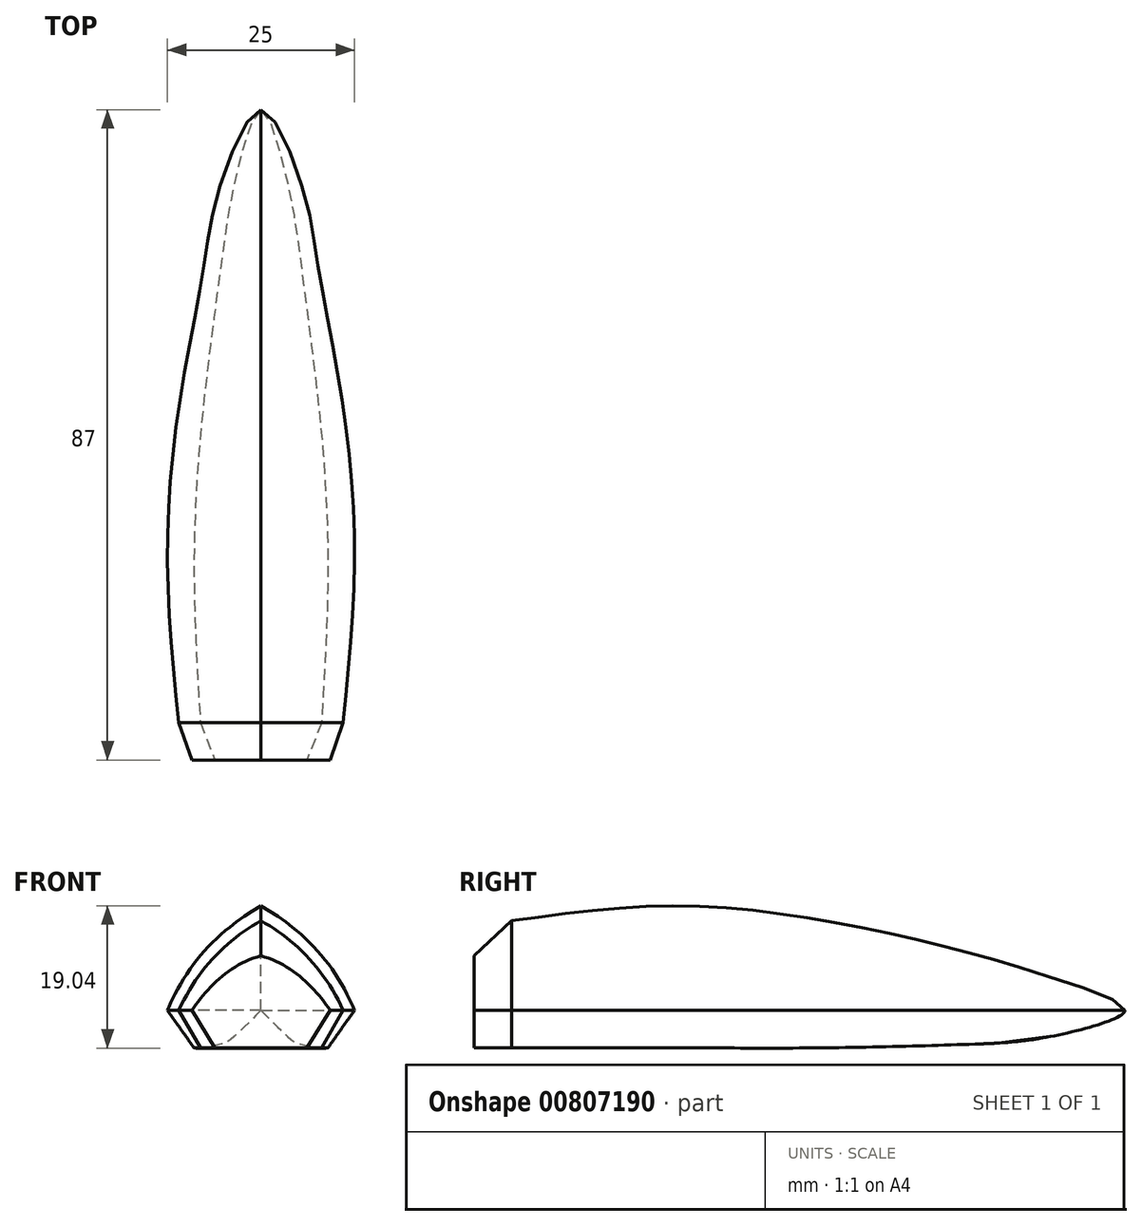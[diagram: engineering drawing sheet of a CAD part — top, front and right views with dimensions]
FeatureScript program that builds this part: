
annotation { "Feature Type Name" : "Feature", "Feature Type Description" : "" }
export const myFeature = defineFeature(function(context is Context, id is Id, definition is map)
    precondition{}
    {
        {
            var Q0;
            Q0=qCreatedBy(makeId("Front.planeOp"),FACE);
            cPlane(context, id + "F0", {"entities" : qUnion([Q0]), "cplaneType" : CPlaneType.OFFSET, "offset" : 43.5 * mm, "oppositeDirection" : true, "width" : 152.4 * mm, "height" : 152.4 * mm});
        }
        {
            var Q0;
            Q0=qCreatedBy(id+"F0.planeOp",FACE);
            cPlane(context, id + "F1", {"entities" : qUnion([Q0]), "cplaneType" : CPlaneType.OFFSET, "offset" : 10 * mm, "width" : 150 * mm, "height" : 150 * mm});
        }
        {
            var Q0;
            Q0=qCreatedBy(id+"F0.planeOp",FACE);
            cPlane(context, id + "F2", {"entities" : qUnion([Q0]), "cplaneType" : CPlaneType.OFFSET, "offset" : 20 * mm, "width" : 150 * mm, "height" : 150 * mm});
        }
        {
            var Q0;
            Q0=qCreatedBy(id+"F0.planeOp",FACE);
            cPlane(context, id + "F3", {"entities" : qUnion([Q0]), "cplaneType" : CPlaneType.OFFSET, "offset" : 40 * mm, "width" : 150 * mm, "height" : 150 * mm});
        }
        {
            var Q0;
            Q0=qCreatedBy(id+"F0.planeOp",FACE);
            cPlane(context, id + "F4", {"entities" : qUnion([Q0]), "cplaneType" : CPlaneType.OFFSET, "offset" : 60 * mm, "width" : 150 * mm, "height" : 150 * mm});
        }
        {
            var Q0;
            Q0=qCreatedBy(id+"F0.planeOp",FACE);
            cPlane(context, id + "F5", {"entities" : qUnion([Q0]), "cplaneType" : CPlaneType.OFFSET, "offset" : 82 * mm, "width" : 150 * mm, "height" : 150 * mm});
        }
        {
            var Q0;
            Q0=qCreatedBy(id+"F0.planeOp",FACE);
            cPlane(context, id + "F6", {"entities" : qUnion([Q0]), "cplaneType" : CPlaneType.OFFSET, "offset" : 87 * mm, "width" : 150 * mm, "height" : 150 * mm});
        }
        {
            var Q0;
            Q0=qCreatedBy(id+"F0.planeOp",FACE);
            var sketch = newSketch(context, id + "F7", { "sketchPlane" : qUnion([Q0])});
            skPoint(sketch, "E0", {"position": v(0, 0) * mm});
            skSolve(sketch);
        }
        {
            var Q0;
            Q0=qCreatedBy(id+"F1.planeOp",FACE);
            var sketch = newSketch(context, id + "F8", { "sketchPlane" : qUnion([Q0])});
            skLineSegment(sketch, "E1", {"start": v(0, -3.5) * mm, "end": v(0, 4.47) * mm, "construction": true});
            skLineSegment(sketch, "E2", {"start": v(5.4, 0) * mm, "end": v(-5.4, 0) * mm, "construction": true});
            skLineSegment(sketch, "E3", {"start": v(5.4, 0) * mm, "end": v(3.6, -3.5) * mm});
            skLineSegment(sketch, "E4", {"start": v(3.6, -3.5) * mm, "end": v(-3.6, -3.5) * mm});
            skLineSegment(sketch, "E5", {"start": v(-3.6, -3.5) * mm, "end": v(-5.4, 0) * mm});
            skPoint(sketch, "E6", {"position": v(0, -3.5) * mm});
            skFitSpline(sketch, "E7", {"points": [v(-5.4, 0) * mm, v(0, 4.47) * mm], "startDerivative": vector(1.5, 3.9) * mm, "endDerivative": vector(9, 1.5) * mm});
            skFitSpline(sketch, "E8.MirrorCS", {"points": [v(5.4, 0) * mm, v(0, 4.47) * mm], "startDerivative": vector(-1.5, 3.9) * mm, "endDerivative": vector(-9, 1.5) * mm});
            skSolve(sketch);
        }
        {
            var Q0;
            Q0=qCreatedBy(id+"F2.planeOp",FACE);
            var sketch = newSketch(context, id + "F9", { "sketchPlane" : qUnion([Q0])});
            skLineSegment(sketch, "E9", {"start": v(0, 7.5) * mm, "end": v(0, -4.5) * mm, "construction": true});
            skLineSegment(sketch, "E10", {"start": v(-7.5, 0) * mm, "end": v(7.5, 0) * mm, "construction": true});
            skLineSegment(sketch, "E11", {"start": v(-7.5, 0) * mm, "end": v(-5.25, -4.5) * mm});
            skLineSegment(sketch, "E12", {"start": v(-5.25, -4.5) * mm, "end": v(5.25, -4.5) * mm});
            skLineSegment(sketch, "E13", {"start": v(5.25, -4.5) * mm, "end": v(7.5, 0) * mm});
            skFitSpline(sketch, "E14", {"points": [v(-7.5, 0) * mm, v(0, 7.5) * mm], "startDerivative": vector(6, 9) * mm, "endDerivative": vector(12, 6) * mm});
            skFitSpline(sketch, "E15.MirrorCS", {"points": [v(7.5, 0) * mm, v(0, 7.5) * mm], "startDerivative": vector(-6, 9) * mm, "endDerivative": vector(-12, 6) * mm});
            skSolve(sketch);
        }
        {
            var Q0;
            Q0=qCreatedBy(id+"F3.planeOp",FACE);
            var sketch = newSketch(context, id + "F10", { "sketchPlane" : qUnion([Q0])});
            skLineSegment(sketch, "E16", {"start": v(0, 11.95) * mm, "end": v(0, -5) * mm, "construction": true});
            skLineSegment(sketch, "E17", {"start": v(-11, 0) * mm, "end": v(11, 0) * mm, "construction": true});
            skLineSegment(sketch, "E18", {"start": v(-11, 0) * mm, "end": v(-7.75, -5) * mm});
            skLineSegment(sketch, "E19", {"start": v(-7.75, -5) * mm, "end": v(7.75, -5) * mm});
            skLineSegment(sketch, "E20", {"start": v(7.75, -5) * mm, "end": v(11, 0) * mm});
            skFitSpline(sketch, "E21", {"points": [v(-11, 0) * mm, v(0, 11.95) * mm], "startDerivative": vector(6, 15) * mm, "endDerivative": vector(15, 7.5) * mm});
            skFitSpline(sketch, "E22.MirrorCS", {"points": [v(11, 0) * mm, v(0, 11.95) * mm], "startDerivative": vector(-6, 15) * mm, "endDerivative": vector(-15, 7.5) * mm});
            skSolve(sketch);
        }
        {
            var Q0;
            Q0=qCreatedBy(id+"F4.planeOp",FACE);
            var sketch = newSketch(context, id + "F11", { "sketchPlane" : qUnion([Q0])});
            skLineSegment(sketch, "E23", {"start": v(-12.5, 0) * mm, "end": v(12.5, 0) * mm, "construction": true});
            skLineSegment(sketch, "E24", {"start": v(0, -5) * mm, "end": v(0, 14) * mm, "construction": true});
            skLineSegment(sketch, "E25", {"start": v(-12.5, 0) * mm, "end": v(-8.95, -5) * mm});
            skLineSegment(sketch, "E26", {"start": v(-8.95, -5) * mm, "end": v(8.95, -5) * mm});
            skLineSegment(sketch, "E27", {"start": v(8.95, -5) * mm, "end": v(12.5, 0) * mm});
            skFitSpline(sketch, "E28", {"points": [v(-12.5, 0) * mm, v(0, 14) * mm], "startDerivative": vector(7.5, 18) * mm, "endDerivative": vector(18, 10.5) * mm});
            skFitSpline(sketch, "E29.MirrorCS", {"points": [v(12.5, 0) * mm, v(0, 14) * mm], "startDerivative": vector(-7.5, 18) * mm, "endDerivative": vector(-18, 10.5) * mm});
            skSolve(sketch);
        }
        {
            var Q0;
            Q0=qCreatedBy(id+"F5.planeOp",FACE);
            var sketch = newSketch(context, id + "F12", { "sketchPlane" : qUnion([Q0])});
            skLineSegment(sketch, "E30", {"start": v(0, 12) * mm, "end": v(0, -5) * mm, "construction": true});
            skLineSegment(sketch, "E31", {"start": v(11, 0) * mm, "end": v(-11, 0) * mm, "construction": true});
            skLineSegment(sketch, "E32", {"start": v(-11, 0) * mm, "end": v(-8.1, -5) * mm});
            skLineSegment(sketch, "E33", {"start": v(-8.1, -5) * mm, "end": v(8.1, -5) * mm});
            skLineSegment(sketch, "E34", {"start": v(8.1, -5) * mm, "end": v(11, 0) * mm});
            skFitSpline(sketch, "E35", {"points": [v(-11, 0) * mm, v(0, 12) * mm], "startDerivative": vector(7.5, 16.5) * mm, "endDerivative": vector(13.5, 7.5) * mm});
            skFitSpline(sketch, "E36.MirrorCS", {"points": [v(11, 0) * mm, v(0, 12) * mm], "startDerivative": vector(-7.5, 16.5) * mm, "endDerivative": vector(-13.5, 7.5) * mm});
            skSolve(sketch);
        }
        {
            var Q0;
            Q0=qCreatedBy(id+"F6.planeOp",FACE);
            var sketch = newSketch(context, id + "F13", { "sketchPlane" : qUnion([Q0])});
            skLineSegment(sketch, "E37", {"start": v(0, 7.3) * mm, "end": v(0, -5) * mm, "construction": true});
            skLineSegment(sketch, "E38", {"start": v(-9.25, 0) * mm, "end": v(9.25, 0) * mm, "construction": true});
            skLineSegment(sketch, "E39", {"start": v(-9.25, 0) * mm, "end": v(-6.15, -5) * mm});
            skLineSegment(sketch, "E40", {"start": v(-6.15, -5) * mm, "end": v(6.15, -5) * mm});
            skLineSegment(sketch, "E41", {"start": v(6.15, -5) * mm, "end": v(9.25, 0) * mm});
            skFitSpline(sketch, "E42", {"points": [v(-9.25, 0) * mm, v(0, 7.3) * mm], "startDerivative": vector(6, 9) * mm, "endDerivative": vector(12, 3) * mm});
            skFitSpline(sketch, "E43.MirrorCS", {"points": [v(9.25, 0) * mm, v(0, 7.3) * mm], "startDerivative": vector(-6, 9) * mm, "endDerivative": vector(-12, 3) * mm});
            skSolve(sketch);
        }
        {
            var Q0;
            Q0=qCreatedBy(makeId("Right.planeOp"),FACE);
            var sketch = newSketch(context, id + "F14", { "sketchPlane" : qUnion([Q0])});
            skPoint(sketch, "E44.0", {"position": v(23.5, 7.5) * mm});
            skPoint(sketch, "E45.0", {"position": v(3.5, 11.95) * mm});
            skPoint(sketch, "E46.0", {"position": v(43.5, 0) * mm});
            skPoint(sketch, "E47.0", {"position": v(-16.5, 14) * mm});
            skPoint(sketch, "E48.0", {"position": v(-38.5, 12) * mm});
            skFitSpline(sketch, "E49", {"points": [v(43.5, 0) * mm, v(23.5, 7.54) * mm, v(3.5, 11.95) * mm, v(-16.5, 14) * mm, v(-38.5, 12) * mm], "startDerivative": vector(-69.58, 39.92) * mm, "endDerivative": vector(-83.95, -26.6) * mm});
            skSolve(sketch);
        }
        {
            var Q0;
            Q0=sQuery(id+"F7.wireOp",VERTEX,"E0");
            var Q1;
            Q1=makeQuery(id+"F8.imprint","IMPRINT",FACE,{"disambiguationData":[TD([[makeQuery(id+"F8.imprint","IMPRINT",EDGE,{"derivedFrom":sQuery(id+"F8.wireOp",EDGE,"E3")}),-1.0]])]});
            var Q2;
            Q2=makeQuery(id+"F9.imprint","IMPRINT",FACE,{"disambiguationData":[TD([[makeQuery(id+"F9.imprint","IMPRINT",EDGE,{"derivedFrom":sQuery(id+"F9.wireOp",EDGE,"E11")}),1.0]])]});
            var Q3;
            Q3=makeQuery(id+"F10.imprint","IMPRINT",FACE,{"disambiguationData":[TD([[makeQuery(id+"F10.imprint","IMPRINT",EDGE,{"derivedFrom":sQuery(id+"F10.wireOp",EDGE,"E18")}),1.0]])]});
            var Q4;
            Q4=makeQuery(id+"F11.imprint","IMPRINT",FACE,{"disambiguationData":[TD([[makeQuery(id+"F11.imprint","IMPRINT",EDGE,{"derivedFrom":sQuery(id+"F11.wireOp",EDGE,"E25")}),1.0]])]});
            var Q5;
            Q5=makeQuery(id+"F12.imprint","IMPRINT",FACE,{"disambiguationData":[TD([[makeQuery(id+"F12.imprint","IMPRINT",EDGE,{"derivedFrom":sQuery(id+"F12.wireOp",EDGE,"E32")}),1.0]])]});
            var Q6;
            Q6=sQuery(id+"F14.wireOp",EDGE,"E49");
            loft(context, id + "F15", {"startCondition" : LoftEndDerivativeType.TANGENT_TO_PROFILE, "startMagnitude" : .8, "sheetProfilesArray" : [{ "sheetProfileEntities" : qUnion([Q0]) }, { "sheetProfileEntities" : qUnion([Q1]) }, { "sheetProfileEntities" : qUnion([Q2]) }, { "sheetProfileEntities" : qUnion([Q3]) }, { "sheetProfileEntities" : qUnion([Q4]) }, { "sheetProfileEntities" : qUnion([Q5]) }], "guidesArray" : [{ "guideEntities" : qUnion([Q6]), "guideDerivativeType" : LoftGuideDerivativeType.DEFAULT, "guideDerivativeMagnitude" : 1 }]});
        }
        {
            var Q1;
            Q1 = qSketchRegion(id + "F12", true);
            var Q2;
            Q2 = qSketchRegion(id + "F13", true);
            loft(context, id + "F16", {"operationType" : NewBodyOperationType.ADD, "sheetProfilesArray" : [{ "sheetProfileEntities" : qUnion([Q1]) }, { "sheetProfileEntities" : qUnion([Q2]) }]});
        }
    });
